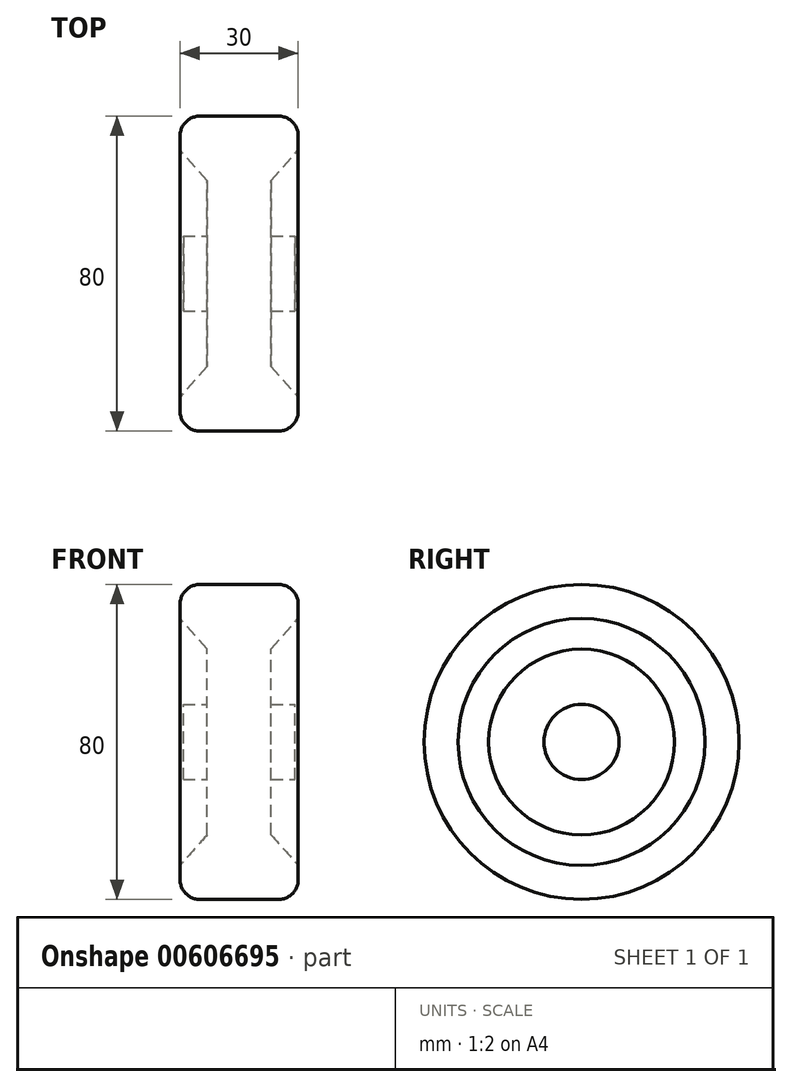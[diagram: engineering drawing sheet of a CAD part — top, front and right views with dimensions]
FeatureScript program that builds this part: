
annotation { "Feature Type Name" : "Feature", "Feature Type Description" : "" }
export const myFeature = defineFeature(function(context is Context, id is Id, definition is map)
    precondition{}
    {
        {
            var Q0;
            Q0=qCreatedBy(makeId("Front.planeOp"),FACE);
            var sketch = newSketch(context, id + "F0", { "sketchPlane" : qUnion([Q0])});
            skLineSegment(sketch, "E0", {"start": v(0, 0) * mm, "end": v(0, 40) * mm});
            skLineSegment(sketch, "E1", {"start": v(0, 40) * mm, "end": v(15, 40) * mm});
            skLineSegment(sketch, "E2", {"start": v(15, 40) * mm, "end": v(15, 31.35) * mm});
            skLineSegment(sketch, "E3", {"start": v(15, 31.35) * mm, "end": v(8.15, 23.6) * mm});
            skLineSegment(sketch, "E4", {"start": v(8.15, 23.6) * mm, "end": v(8.15, 9.55) * mm});
            skLineSegment(sketch, "E5", {"start": v(8.15, 9.55) * mm, "end": v(14.15, 9.55) * mm});
            skLineSegment(sketch, "E6", {"start": v(14.15, 9.55) * mm, "end": v(14.15, 0) * mm});
            skLineSegment(sketch, "E7", {"start": v(14.15, 0) * mm, "end": v(0, 0) * mm});
            skLineSegment(sketch, "E8.MirrorCS", {"start": v(0, 40) * mm, "end": v(-15, 40) * mm});
            skLineSegment(sketch, "E9.MirrorCS", {"start": v(-15, 40) * mm, "end": v(-15, 31.35) * mm});
            skLineSegment(sketch, "E10.MirrorCS", {"start": v(-15, 31.35) * mm, "end": v(-8.15, 23.6) * mm});
            skLineSegment(sketch, "E11.MirrorCS", {"start": v(-8.15, 23.6) * mm, "end": v(-8.15, 9.55) * mm});
            skLineSegment(sketch, "E12.MirrorCS", {"start": v(-8.15, 9.55) * mm, "end": v(-14.15, 9.55) * mm});
            skLineSegment(sketch, "E13.MirrorCS", {"start": v(-14.15, 9.55) * mm, "end": v(-14.15, 0) * mm});
            skLineSegment(sketch, "E14.MirrorCS", {"start": v(-14.15, 0) * mm, "end": v(0, 0) * mm});
            skSolve(sketch);
        }
        {
            var Q0;
            Q0=makeQuery(id+"F0.imprint","IMPRINT",FACE,{"disambiguationData":[TD([[makeQuery(id+"F0.imprint","IMPRINT",EDGE,{"derivedFrom":sQuery(id+"F0.wireOp",EDGE,"E0")}),1.0]])]});
            var Q1;
            Q1=makeQuery(id+"F0.imprint","IMPRINT",FACE,{"disambiguationData":[TD([[makeQuery(id+"F0.imprint","IMPRINT",EDGE,{"derivedFrom":sQuery(id+"F0.wireOp",EDGE,"E0")}),-1.0]])]});
            var Q2;
            Q2=sQuery(id+"F0.wireOp",EDGE,"E7");
            revolve(context, id + "F1", {"entities" : qUnion([Q0, Q1]), "axis" : qUnion([Q2]), "revolveType" : RevolveType.FULL});
        }
        {
            var Q0;
            Q0=makeQuery(id+"F1.opRevolve","SWEPT_EDGE",EDGE,{"disambiguationData":[OSD([sQuery(id+"F0.wireOp",EDGE,"E1"),sQuery(id+"F0.wireOp",EDGE,"E2")])]});
            var Q1;
            Q1=makeQuery(id+"F1.opRevolve","SWEPT_EDGE",EDGE,{"disambiguationData":[OSD([sQuery(id+"F0.wireOp",EDGE,"E8.MirrorCS"),sQuery(id+"F0.wireOp",EDGE,"E9.MirrorCS")])]});
            fillet(context, id + "F2", {"entities" : qUnion([Q0, Q1]), "radius" : 5 * mm, "tangentPropagation" : true, "allowEdgeOverflow" : false});
        }
    });
